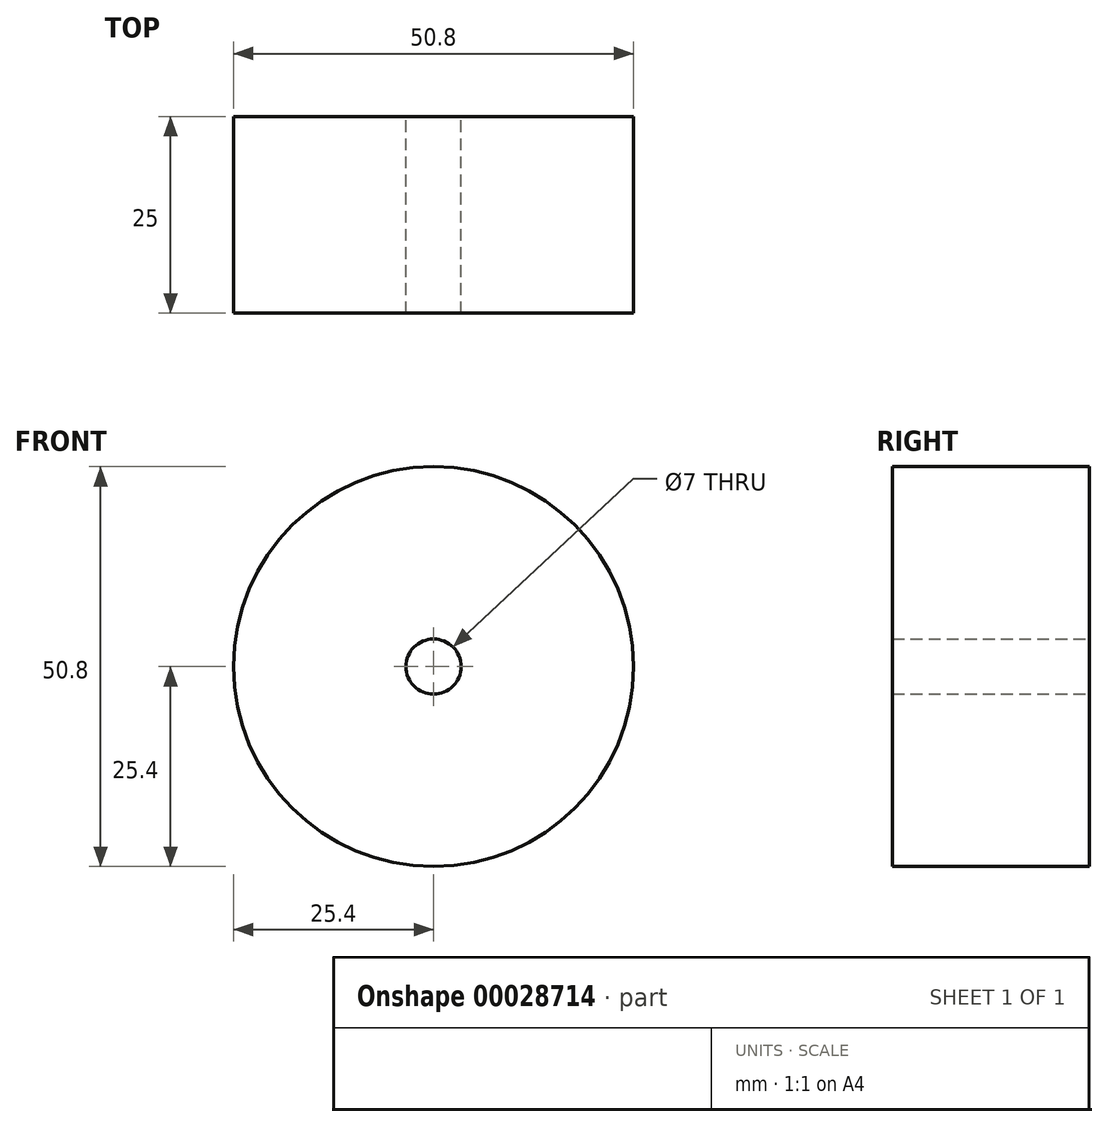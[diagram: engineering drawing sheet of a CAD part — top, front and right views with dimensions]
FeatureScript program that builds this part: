
annotation { "Feature Type Name" : "Feature", "Feature Type Description" : "" }
export const myFeature = defineFeature(function(context is Context, id is Id, definition is map)
    precondition{}
    {
        {
            var Q0;
            Q0=qCreatedBy(makeId("Front.planeOp"),FACE);
            var sketch = newSketch(context, id + "F0", { "sketchPlane" : qUnion([Q0])});
            skCircle(sketch, "E0", {"center": v(0, 0) * mm, "radius": 25.4 * mm});
            skCircle(sketch, "E1", {"center": v(0, 0) * mm, "radius": 3.5 * mm});
            skSolve(sketch);
        }
        {
            var Q0;
            Q0 = qSketchRegion(id + "F0", true);
            extrude(context, id + "F1", {"entities" : qUnion([Q0]), "endBound" : BoundingType.SYMMETRIC, "depth" : 25 * mm, "offsetDistance" : 25 * mm});
        }
    });
